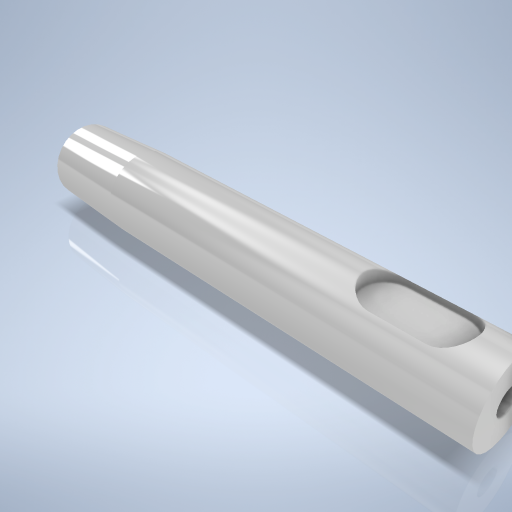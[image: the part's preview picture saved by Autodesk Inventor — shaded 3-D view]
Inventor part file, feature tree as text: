
AUTODESK INVENTOR PART (.ipt)
format: ipt  version: 2024.2 (Build 282272000, 272)  size: 299,008 bytes
history: native  units: mm
features: sketch x3, revolve x1, plane x1, extrude x1, hole x1
ambient origin geometry x8: Origin, YZ Plane, XZ Plane, XY Plane, X Axis, Y Axis, Z Axis, Center Point
bodies: Volumenkörper1 (feature_tree)
feature tree (7):
  revolve  "Umdrehung1"
  plane  "Arbeitsebene1"
  extrude  "Extrusion1"  Depth=58.0mm
  hole  "Bohrung1"  [1 undecoded]
  sketch  "Skizze1"  dims[d0=0.436332mm d1=58.0mm]
  sketch  "Skizze2"  dims[d2=10.0mm d3=11.0mm]
  sketch  "Skizze3"  dims[d4=90.0deg d5=5.0mm d8=12.0mm d9=3.5mm d10=3.0mm d11=1.8mm d12=0.0mm d13=3.242mm d14=8.0mm d15=6.0mm d16=2.5mm d17=90.0deg d18=11.8mm d19=20.594885mm]
note: 1 required parameter value undecoded (feature->parameter linkage not recoverable at this tier; creation-order binding heuristic only, values carry confidence <= 0.55)
